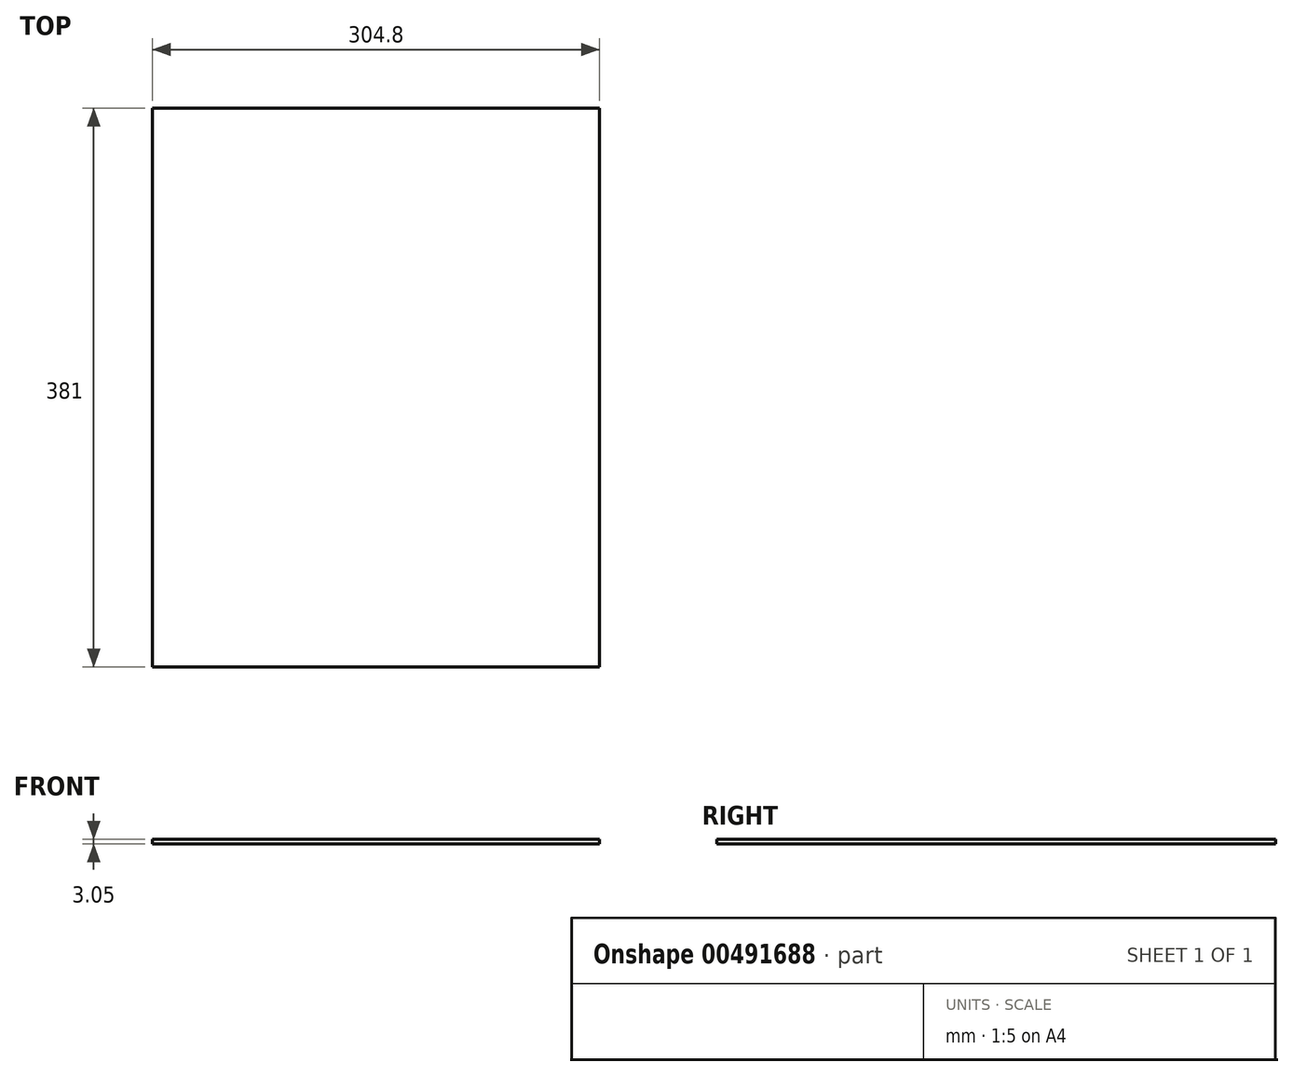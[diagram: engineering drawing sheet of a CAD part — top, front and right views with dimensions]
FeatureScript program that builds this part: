
annotation { "Feature Type Name" : "Feature", "Feature Type Description" : "" }
export const myFeature = defineFeature(function(context is Context, id is Id, definition is map)
    precondition{}
    {
        {
            var Q0;
            Q0=qCreatedBy(makeId("Top.planeOp"),FACE);
            var sketch = newSketch(context, id + "F0", { "sketchPlane" : qUnion([Q0])});
            skLineSegment(sketch, "E0.bottom", {"start": v(-343.23, -60.39) * mm, "end": v(-38.43, -60.39) * mm});
            skLineSegment(sketch, "E0.top", {"start": v(-343.23, -441.39) * mm, "end": v(-38.43, -441.39) * mm});
            skLineSegment(sketch, "E0.left", {"start": v(-343.23, -60.39) * mm, "end": v(-343.23, -441.39) * mm});
            skLineSegment(sketch, "E0.right", {"start": v(-38.43, -60.39) * mm, "end": v(-38.43, -441.39) * mm});
            skSolve(sketch);
        }
        {
            var Q0;
            Q0 = qSketchRegion(id + "F0", true);
            extrude(context, id + "F1", {"entities" : qUnion([Q0]), "depth" : 3.05 * mm});
        }
    });
